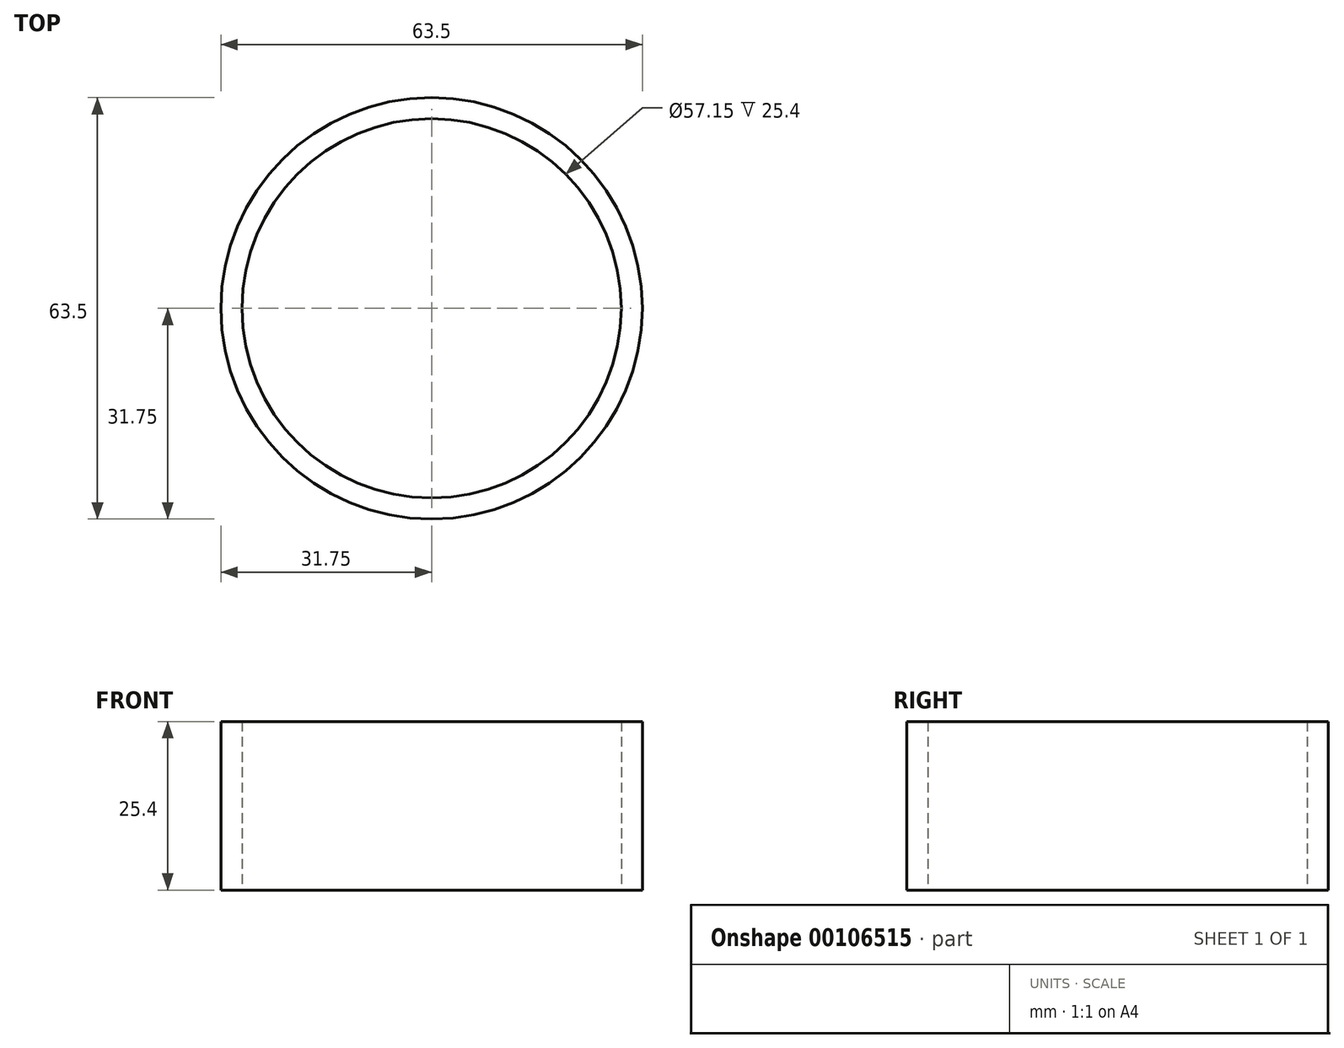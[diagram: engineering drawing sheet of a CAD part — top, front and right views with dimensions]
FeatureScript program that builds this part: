
annotation { "Feature Type Name" : "Feature", "Feature Type Description" : "" }
export const myFeature = defineFeature(function(context is Context, id is Id, definition is map)
    precondition{}
    {
        {
            var Q0;
            Q0=qCreatedBy(makeId("Top.planeOp"),FACE);
            var sketch = newSketch(context, id + "F0", { "sketchPlane" : qUnion([Q0])});
            skCircle(sketch, "E0", {"center": v(0, 0) * mm, "radius": 31.75 * mm});
            skCircle(sketch, "E1", {"center": v(0, 0) * mm, "radius": 28.58 * mm});
            skSolve(sketch);
        }
        {
            var Q0;
            Q0 = qSketchRegion(id + "F0", true);
            extrude(context, id + "F1", {"entities" : qUnion([Q0]), "depth" : 25.4 * mm});
        }
    });
